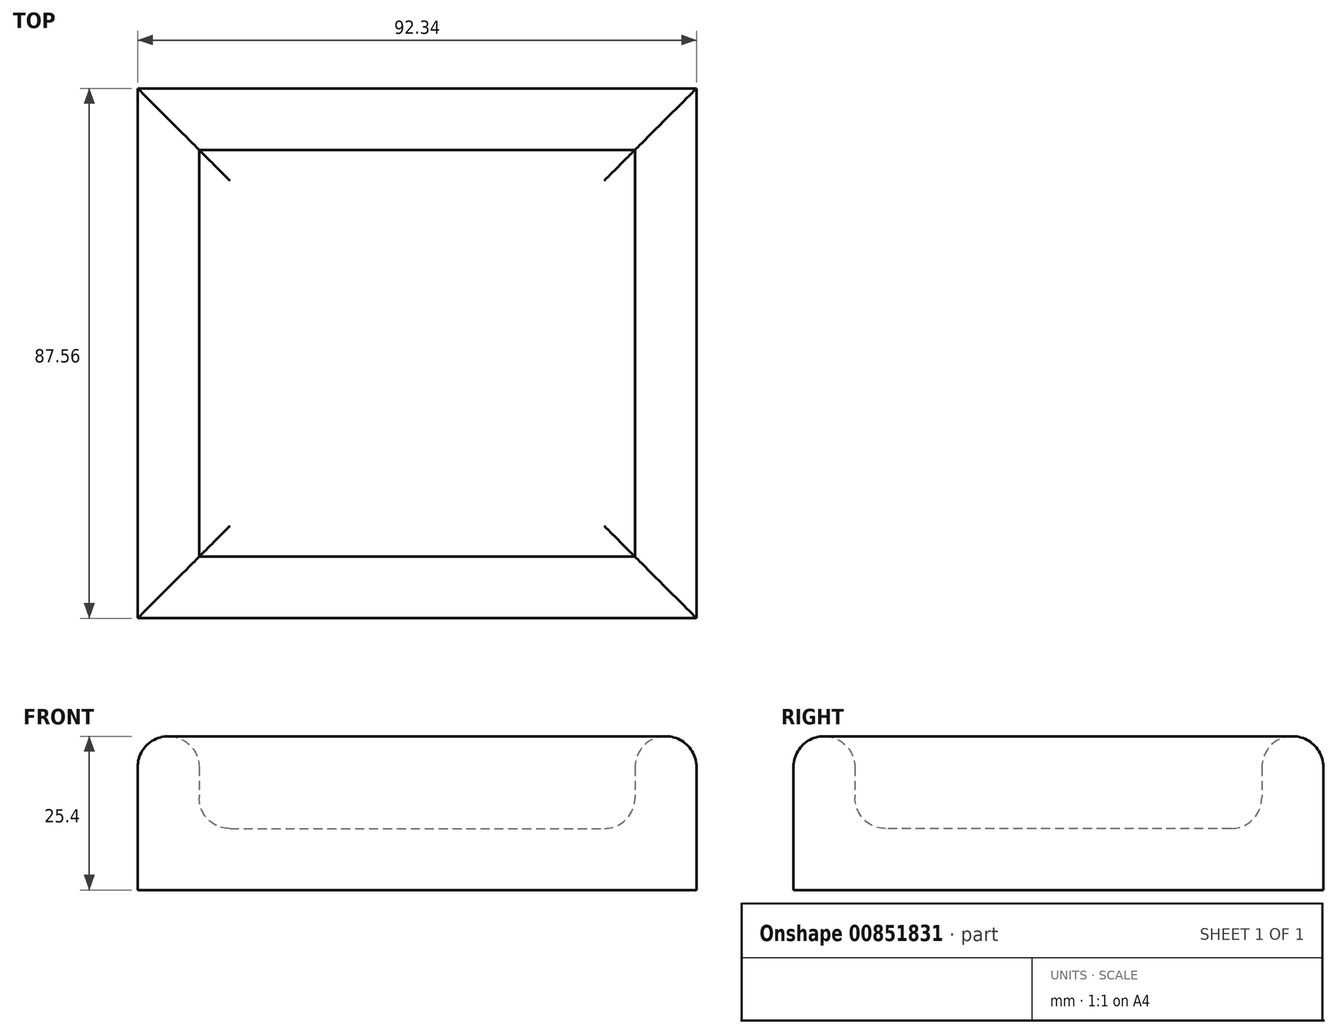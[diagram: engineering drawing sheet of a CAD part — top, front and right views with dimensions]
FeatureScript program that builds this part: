
annotation { "Feature Type Name" : "Feature", "Feature Type Description" : "" }
export const myFeature = defineFeature(function(context is Context, id is Id, definition is map)
    precondition{}
    {
        {
            var Q0;
            Q0=qCreatedBy(makeId("Top.planeOp"),FACE);
            var sketch = newSketch(context, id + "F0", { "sketchPlane" : qUnion([Q0])});
            skLineSegment(sketch, "E0.bottom", {"start": v(-46.36, 42.82) * mm, "end": v(45.98, 42.82) * mm});
            skLineSegment(sketch, "E0.top", {"start": v(-46.36, -44.74) * mm, "end": v(45.98, -44.74) * mm});
            skLineSegment(sketch, "E0.left", {"start": v(-46.36, 42.82) * mm, "end": v(-46.36, -44.74) * mm});
            skLineSegment(sketch, "E0.right", {"start": v(45.98, 42.82) * mm, "end": v(45.98, -44.74) * mm});
            skSolve(sketch);
        }
        {
            var Q0;
            Q0=makeQuery(id+"F0.imprint","IMPRINT",FACE,{"disambiguationData":[TD([[makeQuery(id+"F0.imprint","IMPRINT",EDGE,{"derivedFrom":sQuery(id+"F0.wireOp",EDGE,"E0.bottom")}),-1.0]])]});
            extrude(context, id + "F1", {"entities" : qUnion([Q0]), "depth" : 25.4 * mm, "offsetDistance" : 25.4 * mm});
        }
        {
            var Q0;
            Q0=makeQuery(id+"F1.opExtrude","CAP_FACE",FACE,{"disambiguationData":[OSD([sQuery(id+"F0.wireOp",EDGE,"E0.bottom"),sQuery(id+"F0.wireOp",EDGE,"E0.top"),sQuery(id+"F0.wireOp",EDGE,"E0.left"),sQuery(id+"F0.wireOp",EDGE,"E0.right")])],"isStart":false});
            shell(context, id + "F2", {"entities" : qUnion([Q0]), "thickness" : 10.16 * mm});
        }
        {
            var Q0;
            Q0=makeQuery(id+"F2.opShell","OFFSET_FACE",FACE,{"disambiguationData":[OSD([sQuery(id+"F0.wireOp",EDGE,"E0.bottom"),sQuery(id+"F0.wireOp",EDGE,"E0.top"),sQuery(id+"F0.wireOp",EDGE,"E0.left"),sQuery(id+"F0.wireOp",EDGE,"E0.right")])]});
            var Q1;
            Q1=makeQuery(id+"F1.opExtrude","CAP_FACE",FACE,{"disambiguationData":[OSD([sQuery(id+"F0.wireOp",EDGE,"E0.bottom"),sQuery(id+"F0.wireOp",EDGE,"E0.top"),sQuery(id+"F0.wireOp",EDGE,"E0.left"),sQuery(id+"F0.wireOp",EDGE,"E0.right")])],"isStart":false});
            fillet(context, id + "F3", {"entities" : qUnion([Q0, Q1]), "radius" : 5.08 * mm, "tangentPropagation" : true, "allowEdgeOverflow" : false});
        }
    });
